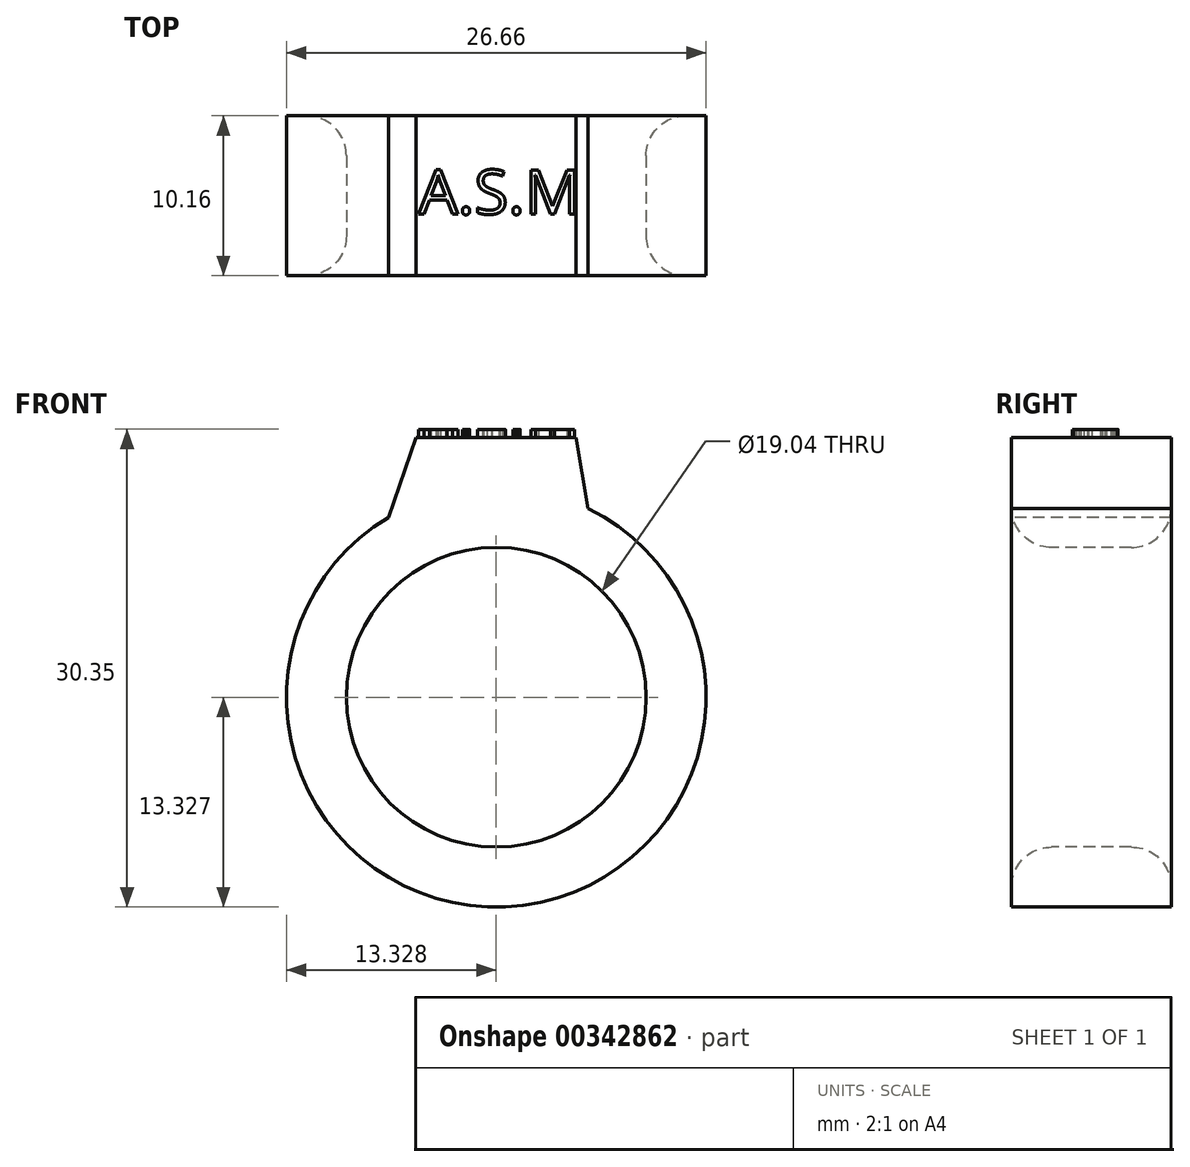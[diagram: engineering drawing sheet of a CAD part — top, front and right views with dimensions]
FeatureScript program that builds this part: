
annotation { "Feature Type Name" : "Feature", "Feature Type Description" : "" }
export const myFeature = defineFeature(function(context is Context, id is Id, definition is map)
    precondition{}
    {
        {
            var Q0;
            Q0=qCreatedBy(makeId("Front.planeOp"),FACE);
            var sketch = newSketch(context, id + "F0", { "sketchPlane" : qUnion([Q0])});
            skCircle(sketch, "E0", {"center": v(-2.48, 13.37) * mm, "radius": 9.52 * mm});
            skCircle(sketch, "E1", {"center": v(-2.48, 13.37) * mm, "radius": 13.33 * mm});
            skSolve(sketch);
        }
        {
            var Q0;
            Q0=makeQuery(id+"F0.imprint","IMPRINT",FACE,{"disambiguationData":[TD([[makeQuery(id+"F0.imprint","IMPRINT",EDGE,{"derivedFrom":sQuery(id+"F0.wireOp",EDGE,"E0")}),-1.0]])]});
            extrude(context, id + "F1", {"entities" : qUnion([Q0]), "oppositeDirection" : true, "depth" : 10.16 * mm});
        }
        {
            var Q0;
            Q0=qCreatedBy(makeId("Front.planeOp"),FACE);
            var sketch = newSketch(context, id + "F2", { "sketchPlane" : qUnion([Q0])});
            skCircle(sketch, "E2.0", {"center": v(-2.48, 13.37) * mm, "radius": 13.33 * mm});
            skLineSegment(sketch, "E3", {"start": v(-9.34, 24.8) * mm, "end": v(-7.56, 29.88) * mm});
            skLineSegment(sketch, "E4", {"start": v(-7.56, 29.88) * mm, "end": v(2.6, 29.88) * mm});
            skLineSegment(sketch, "E5", {"start": v(2.6, 29.88) * mm, "end": v(3.35, 25.35) * mm});
            skLineSegment(sketch, "E6", {"start": v(-2.48, 13.37) * mm, "end": v(-2.48, 49.84) * mm, "construction": true});
            skSolve(sketch);
        }
        {
            var Q0;
            {var subQ0=sQuery(id+"F2.wireOp",EDGE,"E3");Q0=makeQuery(id+"F2.imprint","IMPRINT",FACE,{"disambiguationData":[TD([[makeQuery(id+"F2.imprint","IMPRINT",EDGE,{"derivedFrom":subQ0}),-1.0]])]});}
            extrude(context, id + "F3", {"entities" : qUnion([Q0]), "operationType" : NewBodyOperationType.ADD, "oppositeDirection" : true, "depth" : 10.16 * mm});
        }
        {
            var Q0;
            Q0=makeQuery(id+"F1.opExtrude","CAP_EDGE",EDGE,{"disambiguationData":[OSD([sQuery(id+"F0.wireOp",EDGE,"E0")])],"isStart":true});
            var Q1;
            Q1=makeQuery(id+"F1.opExtrude","CAP_EDGE",EDGE,{"disambiguationData":[OSD([sQuery(id+"F0.wireOp",EDGE,"E0")])],"isStart":false});
            fillet(context, id + "F4", {"entities" : qUnion([Q0, Q1]), "radius" : 2.54 * mm, "tangentPropagation" : true, "allowEdgeOverflow" : false});
        }
        {
            var Q0;
            Q0=makeQuery(id+"F3.opExtrude","SWEPT_FACE",FACE,{"disambiguationData":[OSD([sQuery(id+"F2.wireOp",EDGE,"E4")])]});
            var sketch = newSketch(context, id + "F5", { "sketchPlane" : qUnion([Q0])});
            skText(sketch, "E7", { "text": "A.S.M", "fontName": "OpenSans-Regular.ttf"});
            const initialGuessF5  = {"E7": [-0.00741, 0.00392, 1, 0, 0.00283]};
            skSetInitialGuess(sketch, initialGuessF5);
            skSolve(sketch);
        }
        {
            var Q0;
            Q0 = qSketchRegion(id + "F5", true);
            extrude(context, id + "F6", {"entities" : qUnion([Q0]), "operationType" : NewBodyOperationType.ADD, "depth" : 0.5 * mm});
        }
    });
